# Revit family: Partition_Corflex_5500_Series_Outside_Pocket
name_source: partatom
category: Specialty Equipment
units: mm (PartAtom-declared; Revit-internal decimal feet)

## family parameters
Always vertical = Yes
Classification Number = 23.25.40.17.11
Cut with Voids When Loaded = No
Enable Cutting in Views = No
Maintain Annotation Orientation = No
Part Type = Normal
Room Calculation Point = No
Round Connector Dimension = Use Diameter
Shared = No
Work Plane-Based = No

## types (1)
- Outside Pocket
    Assembly Code = C1010300
    CAD Details = https://www.arcat.com
    CSI MasterFormat = 10 22 39
    CSI MasterFormat 2004 = 10 22 26
    Closure Type Lead = Bulb Seal
    Closure Type Trail = Lever
    Closure Width Lead Standard = 38 mm
    Closure Width Trail = 152 mm
    Default Elevation = 0 mm
    Description = Operable Partition
    Enter Pocket Door Type = 3
    Finish Material Metal = Corflex - Trim - Beige
    Finish Material Panel = Corflex - Vinyl - Blizzard
    Finish Material Pocket Door = Corflex - Vinyl - Blizzard
    Finish Material Track = Corflex - Track - Clear anodized
    Keynote = 10 22 26
    Manufacturer = Corflex, Inc.
    Manufacturer Telephone = 1 877 410-2422 or (1) 450 444-2441
    Model = 5500
    Panel Width Max = 1,219 mm
    Panel Width Min = 533 mm
    Pocket Door Type = 3
    Product Page URL = https://www.arcat.com
    Specification = https://www.arcat.com
    Track Height = 88.9 mm
    Track Width = 127 mm
    Track Width Above = 88.9 mm
    URL = http://www.corflex.ca

## geometry (parser evidence)
native form markers: Sweep x7
no freeform markers — native parametric forms only
